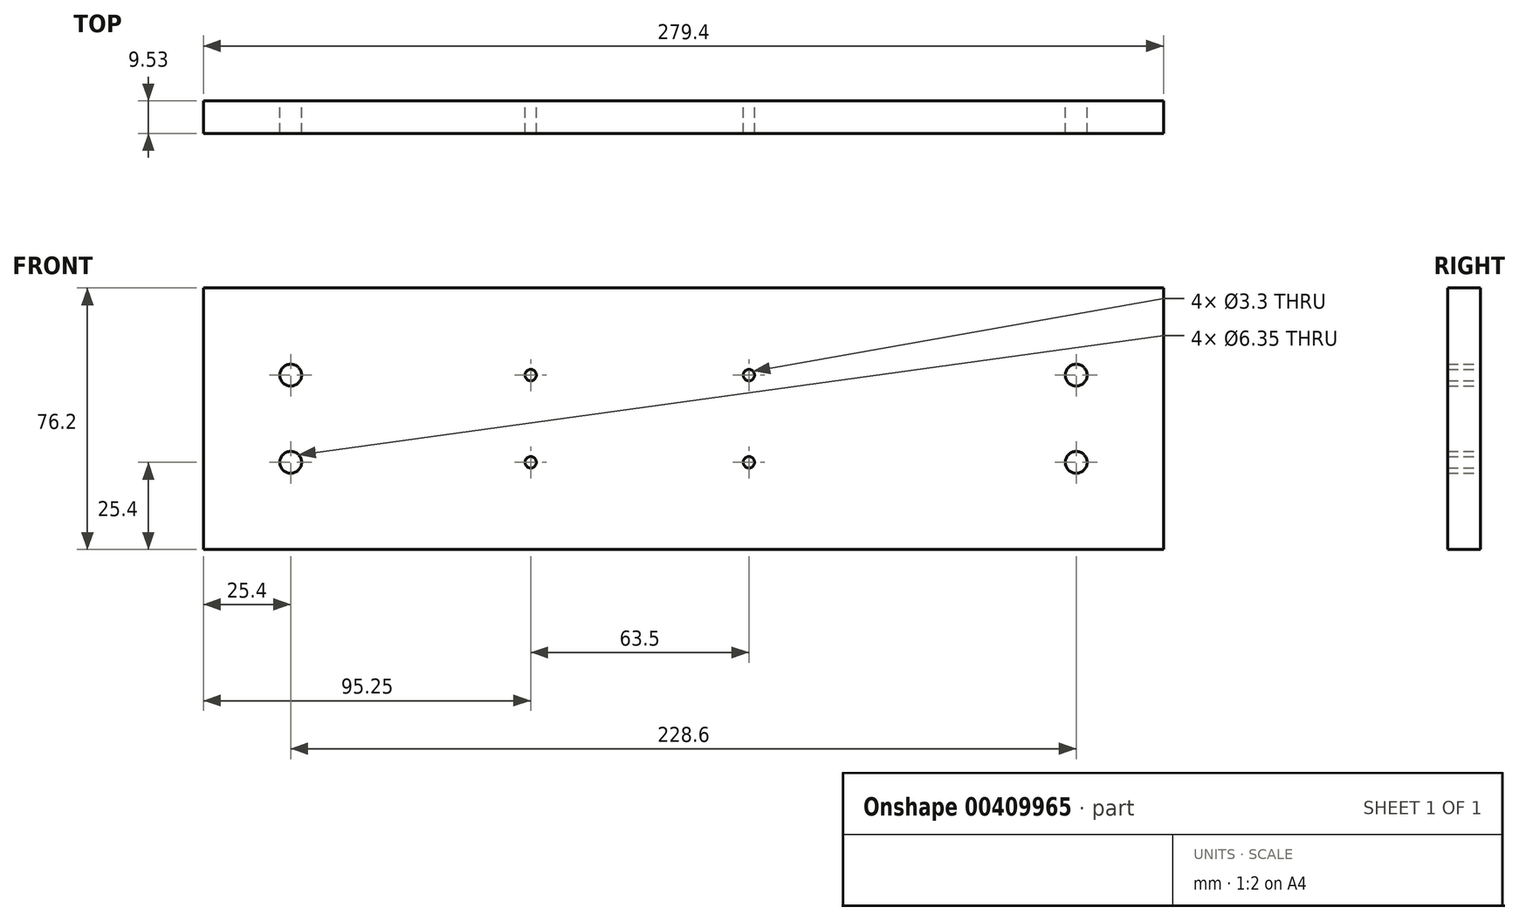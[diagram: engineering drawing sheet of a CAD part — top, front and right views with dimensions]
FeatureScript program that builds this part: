
annotation { "Feature Type Name" : "Feature", "Feature Type Description" : "" }
export const myFeature = defineFeature(function(context is Context, id is Id, definition is map)
    precondition{}
    {
        {
            var Q0;
            Q0=qCreatedBy(makeId("Front.planeOp"),FACE);
            var sketch = newSketch(context, id + "F0", { "sketchPlane" : qUnion([Q0])});
            skLineSegment(sketch, "E0", {"start": v(-139.7, 38.1) * mm, "end": v(139.7, 38.1) * mm});
            skLineSegment(sketch, "E1", {"start": v(-139.7, 38.1) * mm, "end": v(-139.7, -38.1) * mm});
            skLineSegment(sketch, "E2", {"start": v(-139.7, 0) * mm, "end": v(-146.6, 0) * mm});
            skLineSegment(sketch, "E3", {"start": v(0, 38.1) * mm, "end": v(0, 44.53) * mm});
            skLineSegment(sketch, "E4", {"start": v(-139.7, -38.1) * mm, "end": v(139.7, -38.1) * mm});
            skLineSegment(sketch, "E5", {"start": v(139.7, -38.1) * mm, "end": v(139.7, 38.1) * mm});
            skCircle(sketch, "E6", {"center": v(114.3, 12.7) * mm, "radius": 3.18 * mm});
            skCircle(sketch, "E7", {"center": v(114.3, -12.7) * mm, "radius": 3.18 * mm});
            skCircle(sketch, "E8", {"center": v(-114.3, 12.7) * mm, "radius": 3.18 * mm});
            skCircle(sketch, "E9", {"center": v(-114.3, -12.7) * mm, "radius": 3.18 * mm});
            skCircle(sketch, "E10", {"center": v(-44.45, 12.7) * mm, "radius": 1.65 * mm});
            skCircle(sketch, "E11", {"center": v(-44.45, -12.7) * mm, "radius": 1.65 * mm});
            skCircle(sketch, "E12", {"center": v(19.05, 12.7) * mm, "radius": 1.65 * mm});
            skCircle(sketch, "E13", {"center": v(19.05, -12.7) * mm, "radius": 1.65 * mm});
            skSolve(sketch);
        }
        {
            var Q0;
            {var subQ1=sQuery(id+"F0.wireOp",EDGE,"E4");Q0=makeQuery(id+"F0.imprint","IMPRINT",FACE,{"disambiguationData":[TD([[makeQuery(id+"F0.imprint","IMPRINT",EDGE,{"derivedFrom":subQ1}),1.0]])]});}
            extrude(context, id + "F1", {"entities" : qUnion([Q0]), "depth" : 9.52 * mm});
        }
    });
